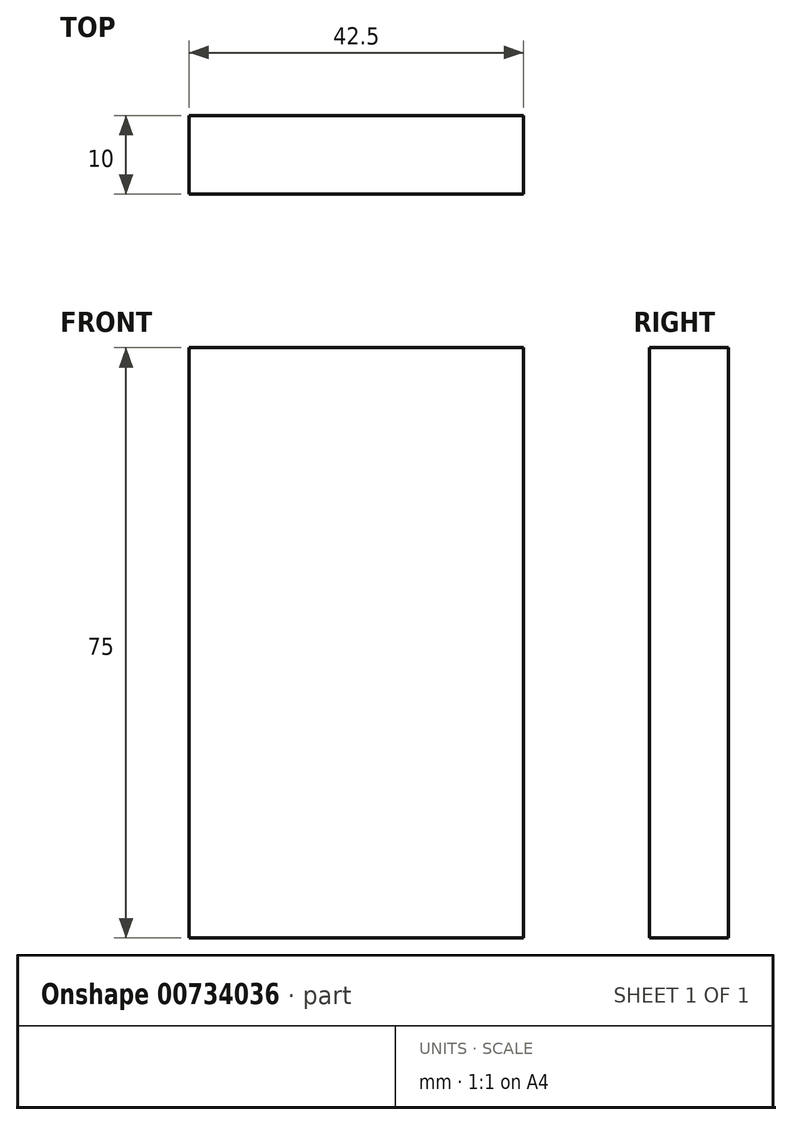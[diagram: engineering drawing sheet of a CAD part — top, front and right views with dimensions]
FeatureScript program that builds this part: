
annotation { "Feature Type Name" : "Feature", "Feature Type Description" : "" }
export const myFeature = defineFeature(function(context is Context, id is Id, definition is map)
    precondition{}
    {
        {
            var Q0;
            Q0=qCreatedBy(makeId("Front.planeOp"),FACE);
            var sketch = newSketch(context, id + "F0", { "sketchPlane" : qUnion([Q0])});
            skLineSegment(sketch, "E0.bottom", {"start": v(-21.1, 41.65) * mm, "end": v(21.4, 41.65) * mm});
            skLineSegment(sketch, "E0.top", {"start": v(-21.1, -33.35) * mm, "end": v(21.4, -33.35) * mm});
            skLineSegment(sketch, "E0.left", {"start": v(-21.1, 41.65) * mm, "end": v(-21.1, -33.35) * mm});
            skLineSegment(sketch, "E0.right", {"start": v(21.4, 41.65) * mm, "end": v(21.4, -33.35) * mm});
            skSolve(sketch);
        }
        {
            var Q0;
            Q0=qSketchRegion(id+"F0",true);
            extrude(context, id + "F1", {"entities" : qUnion([Q0]), "depth" : 10 * mm, "offsetDistance" : 25 * mm});
        }
    });
